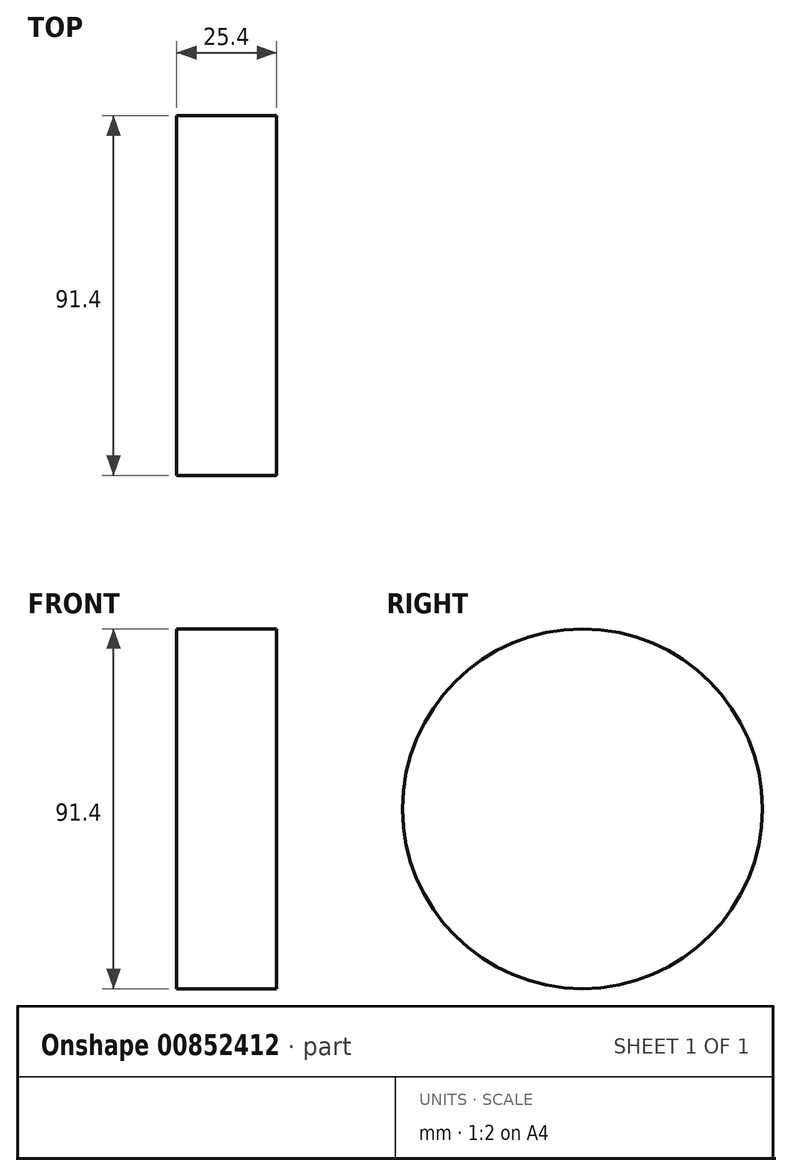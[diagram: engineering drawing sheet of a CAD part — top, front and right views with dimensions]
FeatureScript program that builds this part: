
annotation { "Feature Type Name" : "Feature", "Feature Type Description" : "" }
export const myFeature = defineFeature(function(context is Context, id is Id, definition is map)
    precondition{}
    {
        {
            var Q0;
            Q0=qCreatedBy(makeId("Right.planeOp"),FACE);
            var sketch = newSketch(context, id + "F0", { "sketchPlane" : qUnion([Q0])});
            skCircle(sketch, "E0", {"center": v(0, 0) * mm, "radius": 45.7 * mm});
            skSolve(sketch);
        }
        {
            var Q0;
            Q0 = qSketchRegion(id + "F0", true);
            extrude(context, id + "F1", {"entities" : qUnion([Q0]), "depth" : 25.4 * mm, "offsetDistance" : 25.4 * mm});
        }
    });
